# Revit family: BUILDMAT-SN101015-Lincoln-825-Stainless-Steel
name_source: partatom
category: Plumbing Fixtures
units: mm (PartAtom-declared; Revit-internal decimal feet)

## family parameters
Cut with Voids When Loaded = No
Host = Face
Part Type = Normal
Room Calculation Point = No
Round Connector Dimension = Use Diameter
Shared = No

## types (1)
- Lincoln 825x450x205mm
    Bracket 1 = Yes
    Bracket 2 = Yes
    Bracket 3 = No
    Bracket 4 = Yes
    D. Bracket 1 = 100 mm  [stored 0.328084 ft]
    D. Bracket 2 = 30 mm  [stored 0.0984252 ft]
    D. Bracket 3 = 25 mm  [stored 0.082021 ft]
    D. Bracket 4 = 100 mm  [stored 0.328084 ft]
    D. S. Pad 1 = 230 mm  [stored 0.754593 ft]
    D. S. Pad 2 = 230 mm  [stored 0.754593 ft]
    Default Elevation = 1200 mm
    Depth = 205 mm
    Description = BUILDMAT - Lincoln 825x450 Single & 3/4 Bowl Sink
    Drain Sound Pad 1 = Yes
    Drain Sound Pad 2 = Yes
    Gap = 25 mm  [stored 0.082021 ft]
    Length = 400 mm  [stored 1.31234 ft]
    Manufacturer = BUILDMAT
    Manufacturer URL = https://www.buildmat.com.au
    Material = BUILDMAT Stainless Steel
    Model = SN101015
    Sound Pad 1 = Yes
    Sound Pad 2 = Yes
    URL = https://www.buildmat.com.au
    Width 1 = 450 mm  [stored 1.47638 ft]
    Width 2 = 300 mm

note: [stored X ft] marks values corroborated as IEEE doubles in the binary element streams (Revit-internal decimal feet)

## geometry (parser evidence)
native form markers: Sweep x5
no freeform markers — native parametric forms only
